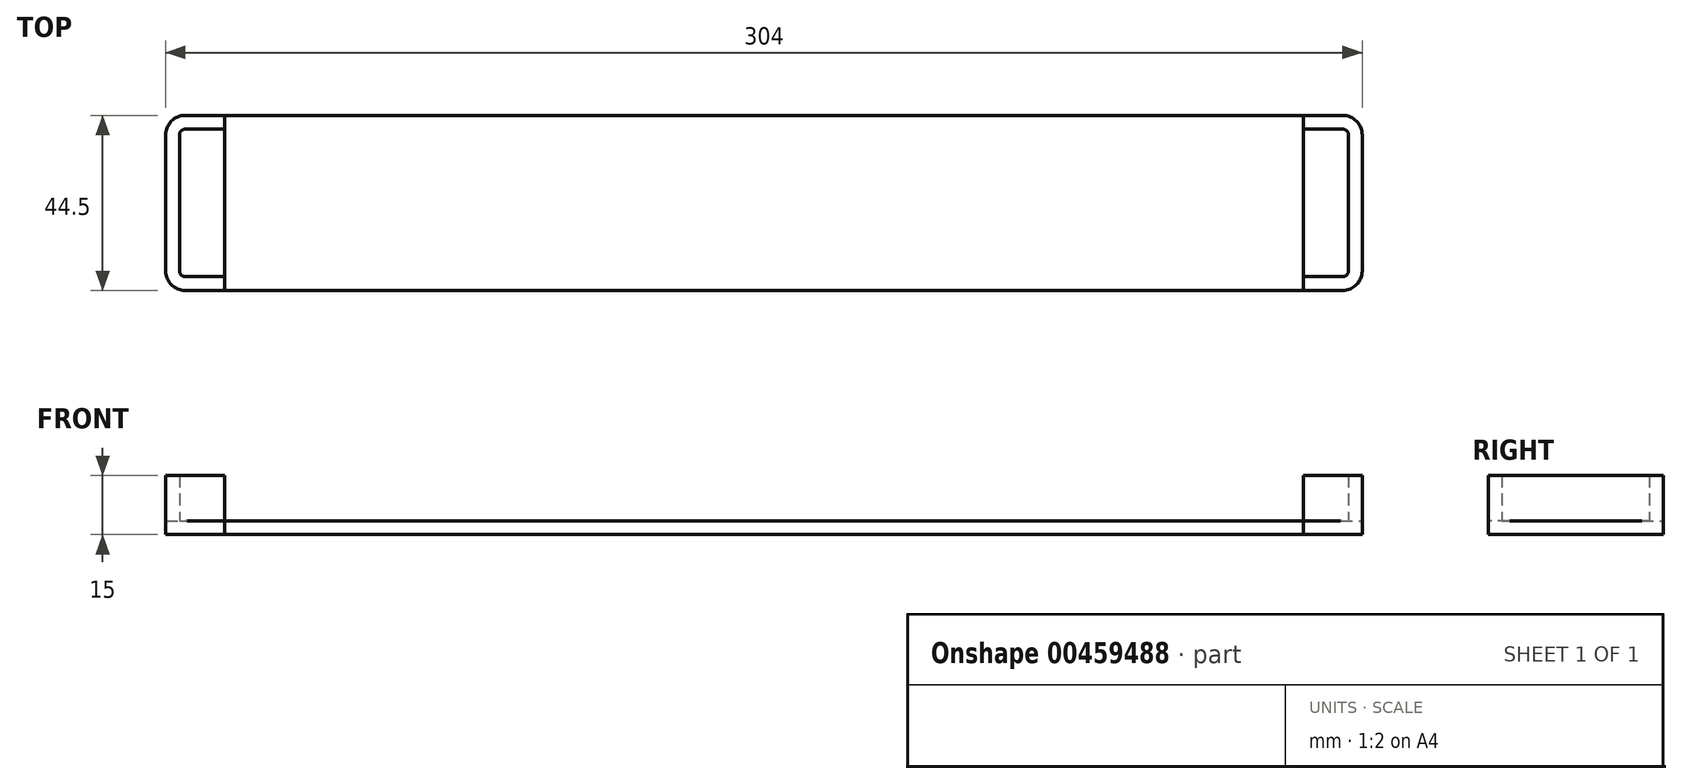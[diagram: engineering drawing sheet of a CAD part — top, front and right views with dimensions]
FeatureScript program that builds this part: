
annotation { "Feature Type Name" : "Feature", "Feature Type Description" : "" }
export const myFeature = defineFeature(function(context is Context, id is Id, definition is map)
    precondition{}
    {
        {
            var Q0;
            Q0=qCreatedBy(makeId("Top.planeOp"),FACE);
            var sketch = newSketch(context, id + "F0", { "sketchPlane" : qUnion([Q0])});
            skLineSegment(sketch, "E0.bottom", {"start": v(152, 22.25) * mm, "end": v(-152, 22.25) * mm});
            skLineSegment(sketch, "E0.top", {"start": v(152, -22.25) * mm, "end": v(-152, -22.25) * mm});
            skLineSegment(sketch, "E0.left", {"start": v(152, 22.25) * mm, "end": v(152, -22.25) * mm});
            skLineSegment(sketch, "E0.right", {"start": v(-152, 22.25) * mm, "end": v(-152, -22.25) * mm});
            skPoint(sketch, "E0.middle", {"position": v(0, 0) * mm});
            skSolve(sketch);
        }
        {
            var Q0;
            Q0=makeQuery(id+"F0.imprint","IMPRINT",FACE,{"disambiguationData":[TD([[makeQuery(id+"F0.imprint","IMPRINT",EDGE,{"derivedFrom":sQuery(id+"F0.wireOp",EDGE,"E0.bottom")}),1.0]])]});
            extrude(context, id + "F1", {"entities" : qUnion([Q0]), "depth" : 3.5 * mm});
        }
        {
            var Q0;
            Q0=makeQuery(id+"F1.opExtrude","SWEPT_EDGE",EDGE,{"disambiguationData":[OSD([sQuery(id+"F0.wireOp",EDGE,"E0.bottom"),sQuery(id+"F0.wireOp",EDGE,"E0.left")])]});
            var Q1;
            Q1=makeQuery(id+"F1.opExtrude","SWEPT_EDGE",EDGE,{"disambiguationData":[OSD([sQuery(id+"F0.wireOp",EDGE,"E0.top"),sQuery(id+"F0.wireOp",EDGE,"E0.left")])]});
            var Q2;
            Q2=makeQuery(id+"F1.opExtrude","SWEPT_EDGE",EDGE,{"disambiguationData":[OSD([sQuery(id+"F0.wireOp",EDGE,"E0.bottom"),sQuery(id+"F0.wireOp",EDGE,"E0.right")])]});
            var Q3;
            Q3=makeQuery(id+"F1.opExtrude","SWEPT_EDGE",EDGE,{"disambiguationData":[OSD([sQuery(id+"F0.wireOp",EDGE,"E0.top"),sQuery(id+"F0.wireOp",EDGE,"E0.right")])]});
            fillet(context, id + "F2", {"entities" : qUnion([Q0, Q1, Q2, Q3]), "radius" : 5.5 * mm, "tangentPropagation" : true, "allowEdgeOverflow" : false});
        }
        {
            var Q0;
            Q0 = qSketchRegion(id + "F0", true);
            extrude(context, id + "F3", {"entities" : qUnion([Q0]), "depth" : 15 * mm});
        }
        {
            var Q0;
            Q0=makeQuery(id+"F3.opExtrude","SWEPT_EDGE",EDGE,{"disambiguationData":[OSD([sQuery(id+"F0.wireOp",EDGE,"E0.bottom"),sQuery(id+"F0.wireOp",EDGE,"E0.left")])]});
            var Q1;
            Q1=makeQuery(id+"F3.opExtrude","SWEPT_EDGE",EDGE,{"disambiguationData":[OSD([sQuery(id+"F0.wireOp",EDGE,"E0.top"),sQuery(id+"F0.wireOp",EDGE,"E0.left")])]});
            var Q2;
            Q2=makeQuery(id+"F3.opExtrude","SWEPT_EDGE",EDGE,{"disambiguationData":[OSD([sQuery(id+"F0.wireOp",EDGE,"E0.bottom"),sQuery(id+"F0.wireOp",EDGE,"E0.right")])]});
            var Q3;
            Q3=makeQuery(id+"F3.opExtrude","SWEPT_EDGE",EDGE,{"disambiguationData":[OSD([sQuery(id+"F0.wireOp",EDGE,"E0.top"),sQuery(id+"F0.wireOp",EDGE,"E0.right")])]});
            fillet(context, id + "F4", {"entities" : qUnion([Q0, Q1, Q2, Q3]), "radius" : 5 * mm, "tangentPropagation" : true, "allowEdgeOverflow" : false});
        }
        {
            var Q0;
            Q0=makeQuery(id+"F3.opExtrude","CAP_FACE",FACE,{"disambiguationData":[OSD([sQuery(id+"F0.wireOp",EDGE,"E0.bottom"),sQuery(id+"F0.wireOp",EDGE,"E0.top"),sQuery(id+"F0.wireOp",EDGE,"E0.left"),sQuery(id+"F0.wireOp",EDGE,"E0.right")])],"isStart":false});
            shell(context, id + "F5", {"entities" : qUnion([Q0]), "thickness" : 3.5 * mm});
        }
        {
            var Q0;
            Q0=qCreatedBy(makeId("Top.planeOp"),FACE);
            var sketch = newSketch(context, id + "F6", { "sketchPlane" : qUnion([Q0])});
            skLineSegment(sketch, "E1.bottom", {"start": v(137, 28.08) * mm, "end": v(-137, 28.08) * mm});
            skLineSegment(sketch, "E1.top", {"start": v(137, -28.08) * mm, "end": v(-137, -28.08) * mm});
            skLineSegment(sketch, "E1.left", {"start": v(137, 28.08) * mm, "end": v(137, -28.08) * mm});
            skLineSegment(sketch, "E1.right", {"start": v(-137, 28.08) * mm, "end": v(-137, -28.08) * mm});
            skPoint(sketch, "E1.middle", {"position": v(0, 0) * mm});
            skSolve(sketch);
        }
        {
            var Q0;
            Q0 = qSketchRegion(id + "F6", true);
            extrude(context, id + "F7", {"entities" : qUnion([Q0]), "depth" : 25 * mm});
        }
        {
            var Q0;
            Q0=makeQuery(id+"F7.opExtrude","SWEPT_BODY",BODY,{"disambiguationData":[OSD([sQuery(id+"F6.wireOp",EDGE,"E1.bottom"),sQuery(id+"F6.wireOp",EDGE,"E1.top"),sQuery(id+"F6.wireOp",EDGE,"E1.left"),sQuery(id+"F6.wireOp",EDGE,"E1.right")])]});
            var Q1;
            Q1=makeQuery(id+"F3.opExtrude","SWEPT_BODY",BODY,{"disambiguationData":[OSD([sQuery(id+"F0.wireOp",EDGE,"E0.bottom"),sQuery(id+"F0.wireOp",EDGE,"E0.top"),sQuery(id+"F0.wireOp",EDGE,"E0.left"),sQuery(id+"F0.wireOp",EDGE,"E0.right")])]});
            booleanBodies(context, id + "F8", {"operationType" : BooleanOperationType.SUBTRACTION, "tools" : qUnion([Q0]), "targets" : qUnion([Q1])});
        }
    });
